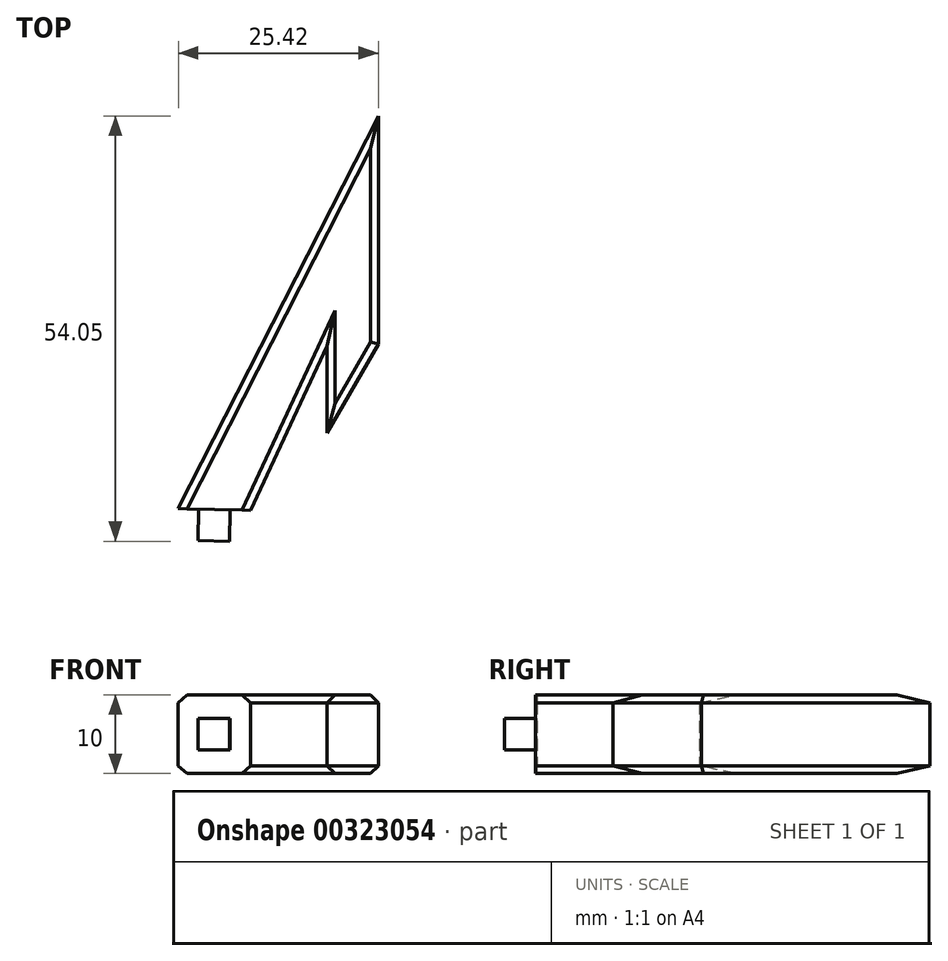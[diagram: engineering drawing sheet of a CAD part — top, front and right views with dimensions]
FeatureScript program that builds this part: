
annotation { "Feature Type Name" : "Feature", "Feature Type Description" : "" }
export const myFeature = defineFeature(function(context is Context, id is Id, definition is map)
    precondition{}
    {
        {
            var Q0;
            Q0=qCreatedBy(makeId("Top.planeOp"),FACE);
            var sketch = newSketch(context, id + "F0", { "sketchPlane" : qUnion([Q0])});
            skLineSegment(sketch, "E0", {"start": v(0, 0) * mm, "end": v(0, 11) * mm});
            skLineSegment(sketch, "E1", {"start": v(0, 0) * mm, "end": v(6.5, 11.26) * mm});
            skLineSegment(sketch, "E2", {"start": v(6.5, 11.26) * mm, "end": v(6.5, 40.26) * mm});
            skLineSegment(sketch, "E3", {"start": v(0, 11) * mm, "end": v(-9.72, -9.85) * mm});
            skLineSegment(sketch, "E4", {"start": v(6.5, 40.26) * mm, "end": v(-18.92, -9.64) * mm});
            skLineSegment(sketch, "E5", {"start": v(-9.72, -9.85) * mm, "end": v(-18.92, -9.64) * mm});
            skSolve(sketch);
        }
        {
            var Q0;
            Q0=makeQuery(id+"F0.imprint","IMPRINT",FACE,{"disambiguationData":[TD([[makeQuery(id+"F0.imprint","IMPRINT",EDGE,{"derivedFrom":sQuery(id+"F0.wireOp",EDGE,"E0")}),-1.0]])]});
            extrude(context, id + "F1", {"entities" : qUnion([Q0]), "depth" : 10 * mm});
        }
        {
            var Q0;
            Q0=makeQuery(id+"F1.opExtrude","SWEPT_FACE",FACE,{"disambiguationData":[OSD([sQuery(id+"F0.wireOp",EDGE,"E5")])]});
            var sketch = newSketch(context, id + "F2", { "sketchPlane" : qUnion([Q0])});
            skLineSegment(sketch, "E6.bottom", {"start": v(-12.1, 7) * mm, "end": v(-16.1, 7) * mm});
            skLineSegment(sketch, "E6.top", {"start": v(-12.1, 3) * mm, "end": v(-16.1, 3) * mm});
            skLineSegment(sketch, "E6.left", {"start": v(-12.1, 7) * mm, "end": v(-12.1, 3) * mm});
            skLineSegment(sketch, "E6.right", {"start": v(-16.1, 7) * mm, "end": v(-16.1, 3) * mm});
            skPoint(sketch, "E6.middle", {"position": v(-14.1, 5) * mm});
            skPoint(sketch, "E6.middle.positionSnap0", {"position": v(-18.7, 5) * mm});
            skPoint(sketch, "E6.middle.positionSnap1", {"position": v(-14.1, 0) * mm});
            skPoint(sketch, "E6.centerSnap0", {"position": v(-18.7, 5) * mm});
            skPoint(sketch, "E6.centerSnap1", {"position": v(-14.1, 0) * mm});
            skSolve(sketch);
        }
        {
            var Q0;
            Q0=makeQuery(id+"F2.imprint","IMPRINT",FACE,{"disambiguationData":[TD([[makeQuery(id+"F2.imprint","IMPRINT",EDGE,{"derivedFrom":sQuery(id+"F2.wireOp",EDGE,"E6.bottom")}),1.0]])]});
            extrude(context, id + "F3", {"entities" : qUnion([Q0]), "operationType" : NewBodyOperationType.ADD, "depth" : 4 * mm});
        }
        {
            var Q0;
            Q0=makeQuery(id+"F1.opExtrude","CAP_EDGE",EDGE,{"disambiguationData":[OSD([sQuery(id+"F0.wireOp",EDGE,"E3")])],"isStart":false});
            var Q1;
            Q1=makeQuery(id+"F1.opExtrude","CAP_EDGE",EDGE,{"disambiguationData":[OSD([sQuery(id+"F0.wireOp",EDGE,"E0")])],"isStart":false});
            var Q2;
            Q2=makeQuery(id+"F1.opExtrude","CAP_EDGE",EDGE,{"disambiguationData":[OSD([sQuery(id+"F0.wireOp",EDGE,"E1")])],"isStart":false});
            var Q3;
            Q3=makeQuery(id+"F1.opExtrude","CAP_EDGE",EDGE,{"disambiguationData":[OSD([sQuery(id+"F0.wireOp",EDGE,"E2")])],"isStart":false});
            var Q4;
            Q4=makeQuery(id+"F1.opExtrude","CAP_EDGE",EDGE,{"disambiguationData":[OSD([sQuery(id+"F0.wireOp",EDGE,"E4")])],"isStart":false});
            var Q5;
            Q5=makeQuery(id+"F1.opExtrude","CAP_EDGE",EDGE,{"disambiguationData":[OSD([sQuery(id+"F0.wireOp",EDGE,"E2")])],"isStart":true});
            var Q6;
            Q6=makeQuery(id+"F1.opExtrude","CAP_EDGE",EDGE,{"disambiguationData":[OSD([sQuery(id+"F0.wireOp",EDGE,"E4")])],"isStart":true});
            var Q7;
            Q7=makeQuery(id+"F1.opExtrude","CAP_EDGE",EDGE,{"disambiguationData":[OSD([sQuery(id+"F0.wireOp",EDGE,"E1")])],"isStart":true});
            var Q8;
            Q8=makeQuery(id+"F1.opExtrude","CAP_EDGE",EDGE,{"disambiguationData":[OSD([sQuery(id+"F0.wireOp",EDGE,"E0")])],"isStart":true});
            var Q9;
            Q9=makeQuery(id+"F1.opExtrude","CAP_EDGE",EDGE,{"disambiguationData":[OSD([sQuery(id+"F0.wireOp",EDGE,"E3")])],"isStart":true});
            chamfer(context, id + "F4", {"entities" : qUnion([Q0, Q1, Q2, Q3, Q4, Q5, Q6, Q7, Q8, Q9]), "width" : 1 * mm, "tangentPropagation" : true});
        }
    });
